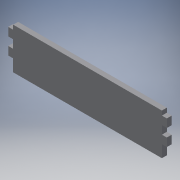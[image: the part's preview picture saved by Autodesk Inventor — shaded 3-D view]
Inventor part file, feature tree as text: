
AUTODESK INVENTOR PART (.ipt)
format: ipt  version: 2019 (Build 230136000, 136)  size: 133,632 bytes
history: native  units: mm
features: reference x11, other x4, extrude x2, sketch x2, projected_geometry x1
ambient origin geometry x8: Origin, YZ Plane, XZ Plane, XY Plane, X Axis, Y Axis, Z Axis, Center Point
bodies: Body1 (feature_tree)
feature tree (20):
  other  "Твердое тело1"
  extrude  "Выдавливание1"  Depth=6.0mm TaperAngle=0.0deg
  extrude  "Выдавливание2"  Depth=6.0mm TaperAngle=0.0deg
  sketch  "Эскиз1"
  reference  "Ссылка1"
  reference  "Ссылка2"
  reference  "Ссылка3"
  reference  "Ссылка4"
  reference  "Ссылка5"
  reference  "Ссылка6"
  reference  "Ссылка7"
  reference  "Ссылка8"
  reference  "Ссылка9"
  sketch  "Эскиз3"
  projected_geometry  "Спроецированная петля1"
  reference  "Ссылка12"
  reference  "Ссылка13"
  other  "Сборка2"
  other  "боковина:2"
  other  "боковина:1"
